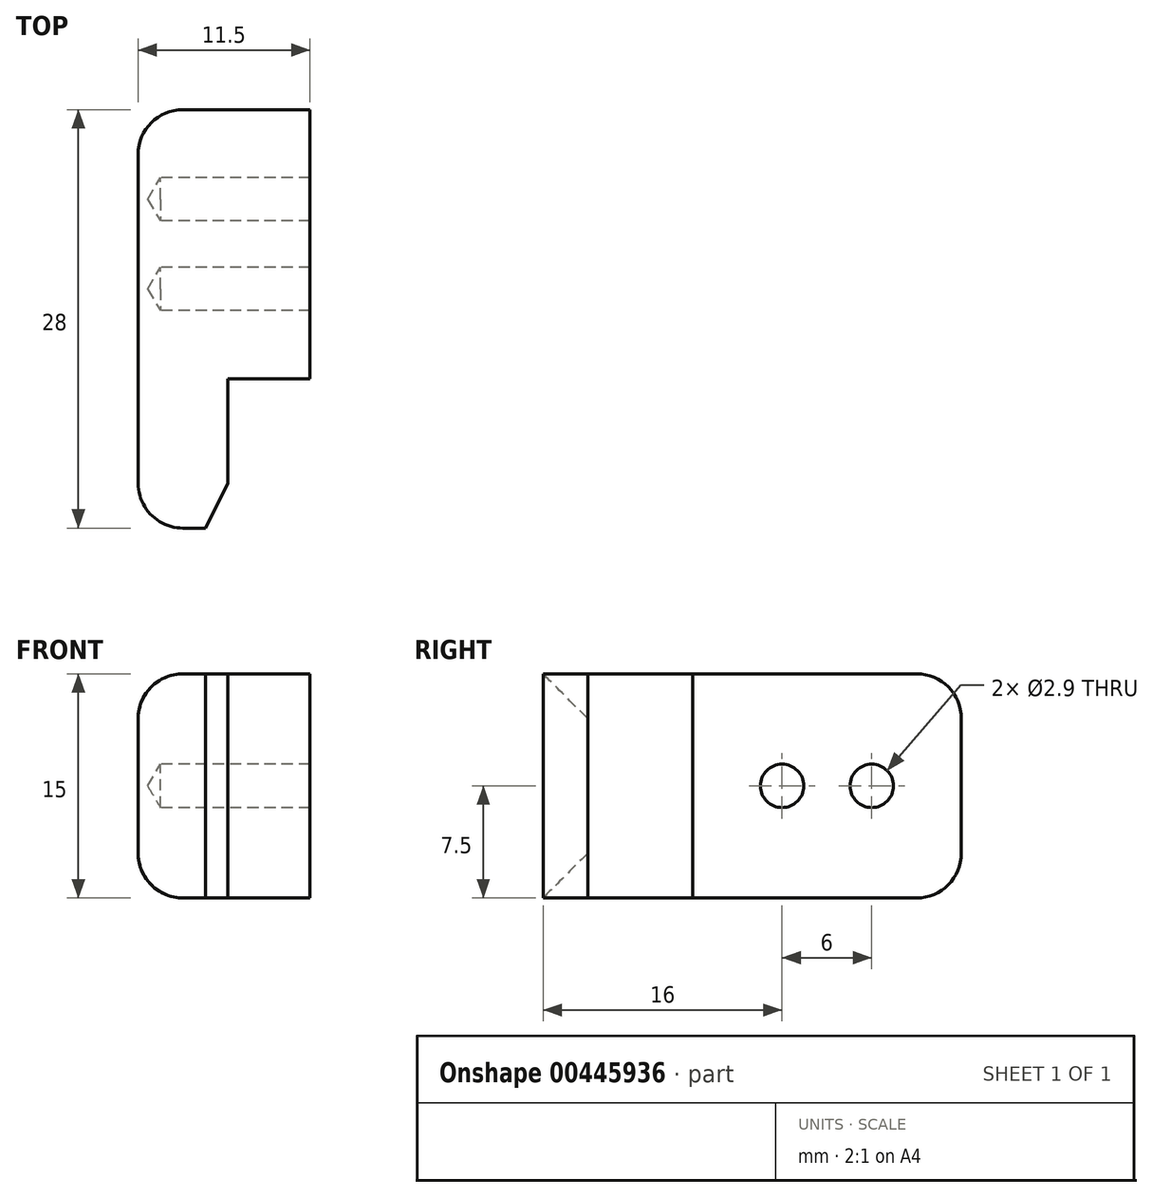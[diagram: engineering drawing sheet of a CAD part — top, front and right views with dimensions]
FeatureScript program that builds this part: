
annotation { "Feature Type Name" : "Feature", "Feature Type Description" : "" }
export const myFeature = defineFeature(function(context is Context, id is Id, definition is map)
    precondition{}
    {
        {
            var Q0;
            Q0=qCreatedBy(makeId("Top.planeOp"),FACE);
            var sketch = newSketch(context, id + "F0", { "sketchPlane" : qUnion([Q0])});
            skLineSegment(sketch, "E0", {"start": v(5.5, 0) * mm, "end": v(5.5, 18) * mm});
            skLineSegment(sketch, "E1", {"start": v(5.5, 18) * mm, "end": v(-6, 18) * mm});
            skLineSegment(sketch, "E2", {"start": v(5.5, 0) * mm, "end": v(0, 0) * mm});
            skLineSegment(sketch, "E3", {"start": v(0, 0) * mm, "end": v(0, -10) * mm});
            skLineSegment(sketch, "E4", {"start": v(0, -10) * mm, "end": v(-6, -10) * mm});
            skLineSegment(sketch, "E5", {"start": v(-6, -10) * mm, "end": v(-6, 18) * mm});
            skSolve(sketch);
        }
        {
            var Q0;
            Q0=makeQuery(id+"F0.imprint","IMPRINT",FACE,{"disambiguationData":[TD([[makeQuery(id+"F0.imprint","IMPRINT",EDGE,{"derivedFrom":sQuery(id+"F0.wireOp",EDGE,"E0")}),1.0]])]});
            extrude(context, id + "F1", {"entities" : qUnion([Q0]), "depth" : 15 * mm});
        }
        {
            var Q0;
            Q0=makeQuery(id+"F1.opExtrude","SWEPT_FACE",FACE,{"disambiguationData":[OSD([sQuery(id+"F0.wireOp",EDGE,"E0")])]});
            var sketch = newSketch(context, id + "F2", { "sketchPlane" : qUnion([Q0])});
            skPoint(sketch, "E6", {"position": v(12, 7.5) * mm});
            skPoint(sketch, "E7", {"position": v(6, 7.5) * mm});
            skSolve(sketch);
        }
        {
            var Q0;
            Q0=sQuery(id+"F2.wireOp",VERTEX,"E7");
            var Q1;
            Q1=sQuery(id+"F2.wireOp",VERTEX,"E6");
            var Q2;
            Q2=makeQuery(id+"F1.opExtrude","SWEPT_BODY",BODY,{"disambiguationData":[OSD([sQuery(id+"F0.wireOp",EDGE,"E0"),sQuery(id+"F0.wireOp",EDGE,"wmPubevF-7naH-zxth-oTlP-scHqGgahTRvK"),sQuery(id+"F0.wireOp",EDGE,"LdkAS8UM-E10D-JGZE-wtYu-DMXdp7MSH5w7"),sQuery(id+"F0.wireOp",EDGE,"E1"),sQuery(id+"F0.wireOp",EDGE,"E2"),sQuery(id+"F0.wireOp",EDGE,"E3"),sQuery(id+"F0.wireOp",EDGE,"E4"),sQuery(id+"F0.wireOp",EDGE,"E5")])]});
            hole(context, id + "F3", {"style" : HoleStyle.SIMPLE, "endStyle" : HoleEndStyle.BLIND, "holeDiameter" : 2.9 * mm, "holeDepth" : 10 * mm, "isTappedThrough" : true, "tappedDepth" : 12 * mm, "tapClearance" : 3, "locations" : qUnion([Q0, Q1]), "scope" : qUnion([Q2]), "startStyle" : HoleStartStyle.SKETCH});
        }
        {
            var Q0;
            Q0=makeQuery(id+"F1.opExtrude","SWEPT_EDGE",EDGE,{"disambiguationData":[OSD([sQuery(id+"F0.wireOp",EDGE,"E3"),sQuery(id+"F0.wireOp",EDGE,"E4")])]});
            chamfer(context, id + "F4", {"entities" : qUnion([Q0]), "chamferType" : ChamferType.TWO_OFFSETS, "width1" : 1.5 * mm, "oppositeDirection" : true, "width2" : 3 * mm, "tangentPropagation" : true});
        }
        {
            var Q0;
            Q0=makeQuery(id+"F1.opExtrude","CAP_EDGE",EDGE,{"disambiguationData":[OSD([sQuery(id+"F0.wireOp",EDGE,"E1")])],"isStart":false});
            var Q1;
            Q1=makeQuery(id+"F1.opExtrude","CAP_EDGE",EDGE,{"disambiguationData":[OSD([sQuery(id+"F0.wireOp",EDGE,"E1")])],"isStart":true});
            var Q2;
            Q2=makeQuery(id+"F1.opExtrude","SWEPT_EDGE",EDGE,{"disambiguationData":[OSD([sQuery(id+"F0.wireOp",EDGE,"E1"),sQuery(id+"F0.wireOp",EDGE,"E5")])]});
            var Q3;
            Q3=makeQuery(id+"F1.opExtrude","CAP_EDGE",EDGE,{"disambiguationData":[OSD([sQuery(id+"F0.wireOp",EDGE,"E5")])],"isStart":true});
            var Q4;
            Q4=makeQuery(id+"F1.opExtrude","CAP_EDGE",EDGE,{"disambiguationData":[OSD([sQuery(id+"F0.wireOp",EDGE,"E5")])],"isStart":false});
            var Q5;
            Q5=makeQuery(id+"F1.opExtrude","SWEPT_EDGE",EDGE,{"disambiguationData":[OSD([sQuery(id+"F0.wireOp",EDGE,"E4"),sQuery(id+"F0.wireOp",EDGE,"E5")])]});
            fillet(context, id + "F5", {"entities" : qUnion([Q0, Q1, Q2, Q3, Q4, Q5]), "radius" : 3 * mm, "tangentPropagation" : true, "allowEdgeOverflow" : false});
        }
    });
